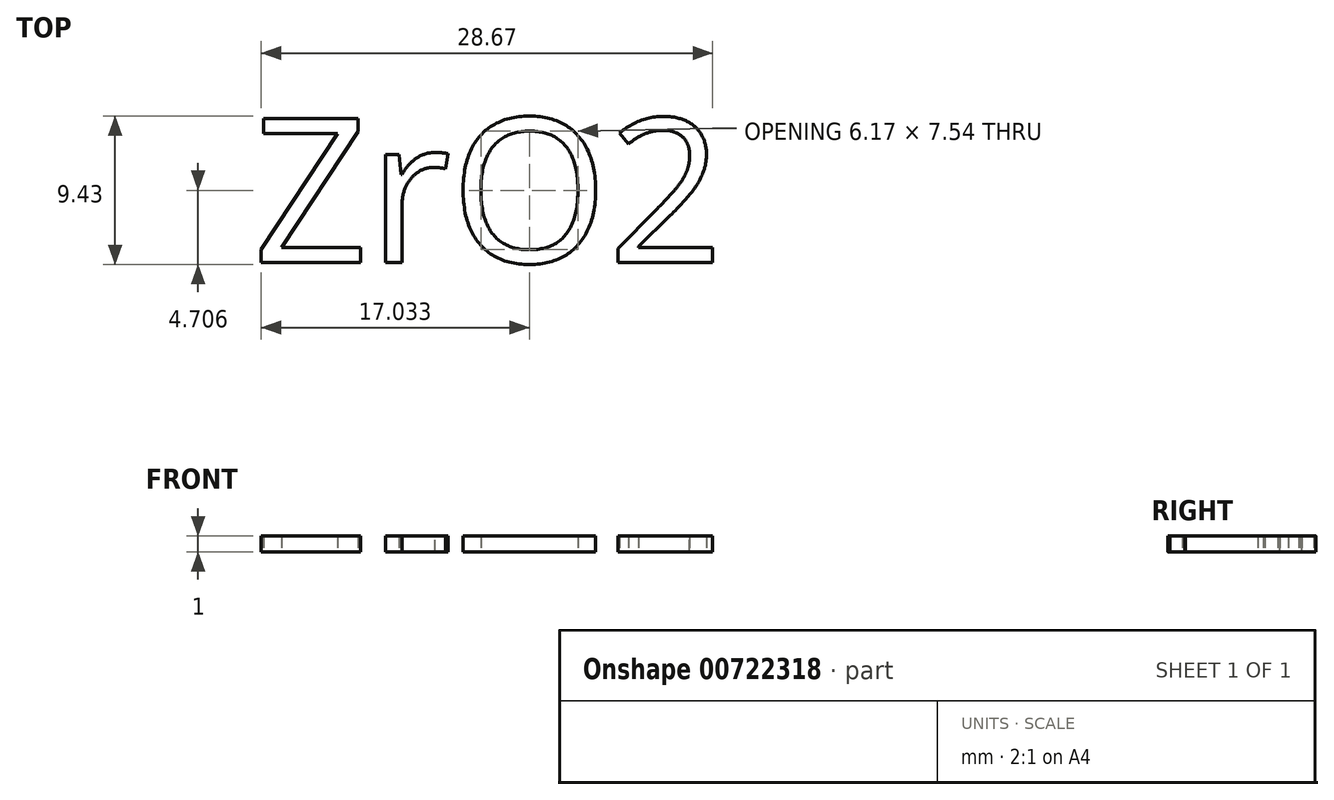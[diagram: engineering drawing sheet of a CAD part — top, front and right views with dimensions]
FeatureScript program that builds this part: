
annotation { "Feature Type Name" : "Feature", "Feature Type Description" : "" }
export const myFeature = defineFeature(function(context is Context, id is Id, definition is map)
    precondition{}
    {
        {
            var Q0;
            Q0=qCreatedBy(makeId("Top.planeOp"),FACE);
            var sketch = newSketch(context, id + "F0", { "sketchPlane" : qUnion([Q0])});
            skText(sketch, "E0", { "text": "ZrO2", "fontName": "OpenSans-Regular.ttf"});
            const initialGuessF0  = {"E0": [-0.01463, -0.00375, 1, 0, 0.00923]};
            skSetInitialGuess(sketch, initialGuessF0);
            skSolve(sketch);
        }
        {
            var Q0;
            Q0 = qSketchRegion(id + "F0", true);
            extrude(context, id + "F1", {"entities" : qUnion([Q0]), "depth" : 1 * mm, "offsetDistance" : 25 * mm});
        }
    });
